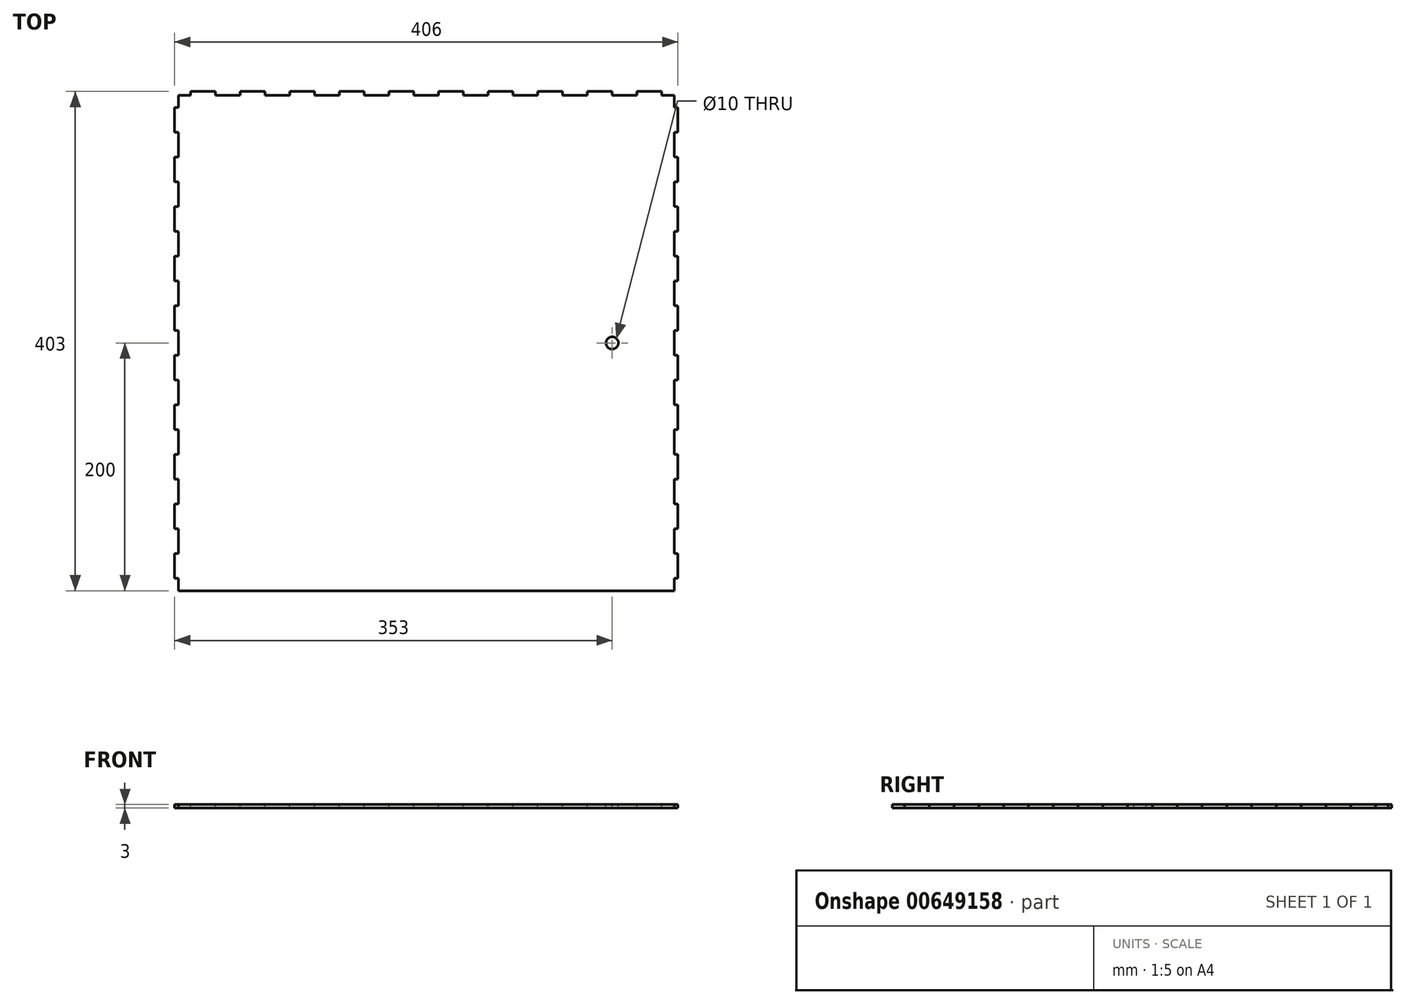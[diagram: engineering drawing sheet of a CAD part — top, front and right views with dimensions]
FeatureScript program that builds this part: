
annotation { "Feature Type Name" : "Feature", "Feature Type Description" : "" }
export const myFeature = defineFeature(function(context is Context, id is Id, definition is map)
    precondition{}
    {
        {
            var Q0;
            Q0=qCreatedBy(makeId("Top.planeOp"),FACE);
            var sketch = newSketch(context, id + "F0", { "sketchPlane" : qUnion([Q0])});
            skLineSegment(sketch, "E0.bottom", {"start": v(200, -200) * mm, "end": v(-200, -200) * mm});
            skLineSegment(sketch, "E0.top", {"start": v(200, 200) * mm, "end": v(-200, 200) * mm});
            skLineSegment(sketch, "E0.left", {"start": v(200, -200) * mm, "end": v(200, 200) * mm});
            skLineSegment(sketch, "E0.right", {"start": v(-200, -200) * mm, "end": v(-200, 200) * mm});
            skPoint(sketch, "E0.middle", {"position": v(0, 0) * mm});
            skSolve(sketch);
        }
        {
            var Q0;
            Q0=makeQuery(id+"F0.imprint","IMPRINT",FACE,{"disambiguationData":[TD([[makeQuery(id+"F0.imprint","IMPRINT",EDGE,{"derivedFrom":sQuery(id+"F0.wireOp",EDGE,"E0.bottom")}),-1.0]])]});
            extrude(context, id + "F1", {"entities" : qUnion([Q0]), "depth" : 3 * mm, "offsetDistance" : 25 * mm});
        }
        {
            var Q0;
            Q0=makeQuery(id+"F1.opExtrude","CAP_FACE",FACE,{"disambiguationData":[OSD([sQuery(id+"F0.wireOp",EDGE,"E0.bottom"),sQuery(id+"F0.wireOp",EDGE,"E0.top"),sQuery(id+"F0.wireOp",EDGE,"E0.left"),sQuery(id+"F0.wireOp",EDGE,"E0.right")])],"isStart":false});
            var sketch = newSketch(context, id + "F2", { "sketchPlane" : qUnion([Q0])});
            skLineSegment(sketch, "E1", {"start": v(-200, -200) * mm, "end": v(-190, -200) * mm, "construction": true});
            skLineSegment(sketch, "E2.bottom", {"start": v(-190, -200) * mm, "end": v(-170, -200) * mm});
            skLineSegment(sketch, "E2.top", {"start": v(-190, -203) * mm, "end": v(-170, -203) * mm});
            skLineSegment(sketch, "E2.left", {"start": v(-190, -200) * mm, "end": v(-190, -203) * mm});
            skLineSegment(sketch, "E2.right", {"start": v(-170, -200) * mm, "end": v(-170, -203) * mm});
            skLineSegment(sketch, "E3.1.0.0", {"start": v(-150, -200) * mm, "end": v(-150, -203) * mm});
            skLineSegment(sketch, "E3.1.0.1", {"start": v(-150, -200) * mm, "end": v(-130, -200) * mm});
            skLineSegment(sketch, "E3.1.0.2", {"start": v(-150, -203) * mm, "end": v(-130, -203) * mm});
            skLineSegment(sketch, "E3.1.0.3", {"start": v(-130, -200) * mm, "end": v(-130, -203) * mm});
            skLineSegment(sketch, "E3.2.0.0", {"start": v(-110, -200) * mm, "end": v(-110, -203) * mm});
            skLineSegment(sketch, "E3.2.0.1", {"start": v(-110, -200) * mm, "end": v(-90, -200) * mm});
            skLineSegment(sketch, "E3.2.0.2", {"start": v(-110, -203) * mm, "end": v(-90, -203) * mm});
            skLineSegment(sketch, "E3.2.0.3", {"start": v(-90, -200) * mm, "end": v(-90, -203) * mm});
            skLineSegment(sketch, "E3.3.0.0", {"start": v(-70, -200) * mm, "end": v(-70, -203) * mm});
            skLineSegment(sketch, "E3.3.0.1", {"start": v(-70, -200) * mm, "end": v(-50, -200) * mm});
            skLineSegment(sketch, "E3.3.0.2", {"start": v(-70, -203) * mm, "end": v(-50, -203) * mm});
            skLineSegment(sketch, "E3.3.0.3", {"start": v(-50, -200) * mm, "end": v(-50, -203) * mm});
            skLineSegment(sketch, "E3.4.0.0", {"start": v(-30, -200) * mm, "end": v(-30, -203) * mm});
            skLineSegment(sketch, "E3.4.0.1", {"start": v(-30, -200) * mm, "end": v(-10, -200) * mm});
            skLineSegment(sketch, "E3.4.0.2", {"start": v(-30, -203) * mm, "end": v(-10, -203) * mm});
            skLineSegment(sketch, "E3.4.0.3", {"start": v(-10, -200) * mm, "end": v(-10, -203) * mm});
            skLineSegment(sketch, "E3.5.0.0", {"start": v(10, -200) * mm, "end": v(10, -203) * mm});
            skLineSegment(sketch, "E3.5.0.1", {"start": v(10, -200) * mm, "end": v(30, -200) * mm});
            skLineSegment(sketch, "E3.5.0.2", {"start": v(10, -203) * mm, "end": v(30, -203) * mm});
            skLineSegment(sketch, "E3.5.0.3", {"start": v(30, -200) * mm, "end": v(30, -203) * mm});
            skLineSegment(sketch, "E3.6.0.0", {"start": v(50, -200) * mm, "end": v(50, -203) * mm});
            skLineSegment(sketch, "E3.6.0.1", {"start": v(50, -200) * mm, "end": v(70, -200) * mm});
            skLineSegment(sketch, "E3.6.0.2", {"start": v(50, -203) * mm, "end": v(70, -203) * mm});
            skLineSegment(sketch, "E3.6.0.3", {"start": v(70, -200) * mm, "end": v(70, -203) * mm});
            skLineSegment(sketch, "E3.7.0.0", {"start": v(90, -200) * mm, "end": v(90, -203) * mm});
            skLineSegment(sketch, "E3.7.0.1", {"start": v(90, -200) * mm, "end": v(110, -200) * mm});
            skLineSegment(sketch, "E3.7.0.2", {"start": v(90, -203) * mm, "end": v(110, -203) * mm});
            skLineSegment(sketch, "E3.7.0.3", {"start": v(110, -200) * mm, "end": v(110, -203) * mm});
            skLineSegment(sketch, "E3.8.0.0", {"start": v(130, -200) * mm, "end": v(130, -203) * mm});
            skLineSegment(sketch, "E3.8.0.1", {"start": v(130, -200) * mm, "end": v(150, -200) * mm});
            skLineSegment(sketch, "E3.8.0.2", {"start": v(130, -203) * mm, "end": v(150, -203) * mm});
            skLineSegment(sketch, "E3.8.0.3", {"start": v(150, -200) * mm, "end": v(150, -203) * mm});
            skLineSegment(sketch, "E3.9.0.0", {"start": v(170, -200) * mm, "end": v(170, -203) * mm});
            skLineSegment(sketch, "E3.9.0.1", {"start": v(170, -200) * mm, "end": v(190, -200) * mm});
            skLineSegment(sketch, "E3.9.0.2", {"start": v(170, -203) * mm, "end": v(190, -203) * mm});
            skLineSegment(sketch, "E3.9.0.3", {"start": v(190, -200) * mm, "end": v(190, -203) * mm});
            skLineSegment(sketch, "E3.direction1", {"start": v(-190, -203) * mm, "end": v(-150, -203) * mm, "construction": true});
            skLineSegment(sketch, "E4.1.0", {"start": v(200, 90) * mm, "end": v(200, 110) * mm});
            skLineSegment(sketch, "E4.1.1", {"start": v(200, 170) * mm, "end": v(203, 170) * mm});
            skLineSegment(sketch, "E4.1.2", {"start": v(200, 10) * mm, "end": v(203, 10) * mm});
            skLineSegment(sketch, "E4.1.3", {"start": v(200, 130) * mm, "end": v(203, 130) * mm});
            skLineSegment(sketch, "E4.1.4", {"start": v(200, -30) * mm, "end": v(203, -30) * mm});
            skLineSegment(sketch, "E4.1.5", {"start": v(203, -190) * mm, "end": v(203, -150) * mm, "construction": true});
            skLineSegment(sketch, "E4.1.6", {"start": v(200, 170) * mm, "end": v(200, 190) * mm});
            skLineSegment(sketch, "E4.1.7", {"start": v(203, 90) * mm, "end": v(203, 110) * mm});
            skLineSegment(sketch, "E4.1.8", {"start": v(200, 10) * mm, "end": v(200, 30) * mm});
            skLineSegment(sketch, "E4.1.9", {"start": v(200, 130) * mm, "end": v(200, 150) * mm});
            skLineSegment(sketch, "E4.1.10", {"start": v(200, -30) * mm, "end": v(200, -10) * mm});
            skLineSegment(sketch, "E4.1.11", {"start": v(200, 50) * mm, "end": v(200, 70) * mm});
            skLineSegment(sketch, "E4.1.12", {"start": v(200, -70) * mm, "end": v(200, -50) * mm});
            skLineSegment(sketch, "E4.1.13", {"start": v(203, -70) * mm, "end": v(203, -50) * mm});
            skLineSegment(sketch, "E4.1.14", {"start": v(200, -190) * mm, "end": v(200, -170) * mm});
            skLineSegment(sketch, "E4.1.15", {"start": v(200, -170) * mm, "end": v(203, -170) * mm});
            skLineSegment(sketch, "E4.1.16", {"start": v(203, 130) * mm, "end": v(203, 150) * mm});
            skLineSegment(sketch, "E4.1.17", {"start": v(203, -30) * mm, "end": v(203, -10) * mm});
            skLineSegment(sketch, "E4.1.18", {"start": v(200, -150) * mm, "end": v(200, -130) * mm});
            skLineSegment(sketch, "E4.1.19", {"start": v(203, -150) * mm, "end": v(203, -130) * mm});
            skLineSegment(sketch, "E4.1.20", {"start": v(200, -130) * mm, "end": v(203, -130) * mm});
            skLineSegment(sketch, "E4.1.21", {"start": v(200, -110) * mm, "end": v(200, -90) * mm});
            skLineSegment(sketch, "E4.1.22", {"start": v(203, -110) * mm, "end": v(203, -90) * mm});
            skLineSegment(sketch, "E4.1.23", {"start": v(200, -90) * mm, "end": v(203, -90) * mm});
            skLineSegment(sketch, "E4.1.24", {"start": v(200, 110) * mm, "end": v(203, 110) * mm});
            skLineSegment(sketch, "E4.1.25", {"start": v(200, -50) * mm, "end": v(203, -50) * mm});
            skLineSegment(sketch, "E4.1.26", {"start": v(203, 50) * mm, "end": v(203, 70) * mm});
            skLineSegment(sketch, "E4.1.27", {"start": v(203, 170) * mm, "end": v(203, 190) * mm});
            skLineSegment(sketch, "E4.1.28", {"start": v(203, 10) * mm, "end": v(203, 30) * mm});
            skLineSegment(sketch, "E4.1.29", {"start": v(200, 150) * mm, "end": v(203, 150) * mm});
            skLineSegment(sketch, "E4.1.30", {"start": v(200, -10) * mm, "end": v(203, -10) * mm});
            skLineSegment(sketch, "E4.1.31", {"start": v(200, 90) * mm, "end": v(203, 90) * mm});
            skLineSegment(sketch, "E4.1.32", {"start": v(200, 70) * mm, "end": v(203, 70) * mm});
            skLineSegment(sketch, "E4.1.33", {"start": v(200, 190) * mm, "end": v(203, 190) * mm});
            skLineSegment(sketch, "E4.1.34", {"start": v(200, 30) * mm, "end": v(203, 30) * mm});
            skLineSegment(sketch, "E4.1.35", {"start": v(200, 50) * mm, "end": v(203, 50) * mm});
            skLineSegment(sketch, "E4.1.36", {"start": v(200, -70) * mm, "end": v(203, -70) * mm});
            skLineSegment(sketch, "E4.1.37", {"start": v(203, -190) * mm, "end": v(203, -170) * mm});
            skLineSegment(sketch, "E4.1.38", {"start": v(200, -150) * mm, "end": v(203, -150) * mm});
            skLineSegment(sketch, "E4.1.39", {"start": v(200, -110) * mm, "end": v(203, -110) * mm});
            skLineSegment(sketch, "E4.1.40", {"start": v(200, -200) * mm, "end": v(200, -190) * mm, "construction": true});
            skLineSegment(sketch, "E4.1.41", {"start": v(200, -190) * mm, "end": v(203, -190) * mm});
            skLineSegment(sketch, "E4.2.0", {"start": v(-90, 200) * mm, "end": v(-110, 200) * mm});
            skLineSegment(sketch, "E4.2.1", {"start": v(-170, 200) * mm, "end": v(-170, 203) * mm});
            skLineSegment(sketch, "E4.2.2", {"start": v(-10, 200) * mm, "end": v(-10, 203) * mm});
            skLineSegment(sketch, "E4.2.3", {"start": v(-130, 200) * mm, "end": v(-130, 203) * mm});
            skLineSegment(sketch, "E4.2.4", {"start": v(30, 200) * mm, "end": v(30, 203) * mm});
            skLineSegment(sketch, "E4.2.5", {"start": v(190, 203) * mm, "end": v(150, 203) * mm, "construction": true});
            skLineSegment(sketch, "E4.2.6", {"start": v(-170, 200) * mm, "end": v(-190, 200) * mm});
            skLineSegment(sketch, "E4.2.7", {"start": v(-90, 203) * mm, "end": v(-110, 203) * mm});
            skLineSegment(sketch, "E4.2.8", {"start": v(-10, 200) * mm, "end": v(-30, 200) * mm});
            skLineSegment(sketch, "E4.2.9", {"start": v(-130, 200) * mm, "end": v(-150, 200) * mm});
            skLineSegment(sketch, "E4.2.10", {"start": v(30, 200) * mm, "end": v(10, 200) * mm});
            skLineSegment(sketch, "E4.2.11", {"start": v(-50, 200) * mm, "end": v(-70, 200) * mm});
            skLineSegment(sketch, "E4.2.12", {"start": v(70, 200) * mm, "end": v(50, 200) * mm});
            skLineSegment(sketch, "E4.2.13", {"start": v(70, 203) * mm, "end": v(50, 203) * mm});
            skLineSegment(sketch, "E4.2.14", {"start": v(190, 200) * mm, "end": v(170, 200) * mm});
            skLineSegment(sketch, "E4.2.15", {"start": v(170, 200) * mm, "end": v(170, 203) * mm});
            skLineSegment(sketch, "E4.2.16", {"start": v(-130, 203) * mm, "end": v(-150, 203) * mm});
            skLineSegment(sketch, "E4.2.17", {"start": v(30, 203) * mm, "end": v(10, 203) * mm});
            skLineSegment(sketch, "E4.2.18", {"start": v(150, 200) * mm, "end": v(130, 200) * mm});
            skLineSegment(sketch, "E4.2.19", {"start": v(150, 203) * mm, "end": v(130, 203) * mm});
            skLineSegment(sketch, "E4.2.20", {"start": v(130, 200) * mm, "end": v(130, 203) * mm});
            skLineSegment(sketch, "E4.2.21", {"start": v(110, 200) * mm, "end": v(90, 200) * mm});
            skLineSegment(sketch, "E4.2.22", {"start": v(110, 203) * mm, "end": v(90, 203) * mm});
            skLineSegment(sketch, "E4.2.23", {"start": v(90, 200) * mm, "end": v(90, 203) * mm});
            skLineSegment(sketch, "E4.2.24", {"start": v(-110, 200) * mm, "end": v(-110, 203) * mm});
            skLineSegment(sketch, "E4.2.25", {"start": v(50, 200) * mm, "end": v(50, 203) * mm});
            skLineSegment(sketch, "E4.2.26", {"start": v(-50, 203) * mm, "end": v(-70, 203) * mm});
            skLineSegment(sketch, "E4.2.27", {"start": v(-170, 203) * mm, "end": v(-190, 203) * mm});
            skLineSegment(sketch, "E4.2.28", {"start": v(-10, 203) * mm, "end": v(-30, 203) * mm});
            skLineSegment(sketch, "E4.2.29", {"start": v(-150, 200) * mm, "end": v(-150, 203) * mm});
            skLineSegment(sketch, "E4.2.30", {"start": v(10, 200) * mm, "end": v(10, 203) * mm});
            skLineSegment(sketch, "E4.2.31", {"start": v(-90, 200) * mm, "end": v(-90, 203) * mm});
            skLineSegment(sketch, "E4.2.32", {"start": v(-70, 200) * mm, "end": v(-70, 203) * mm});
            skLineSegment(sketch, "E4.2.33", {"start": v(-190, 200) * mm, "end": v(-190, 203) * mm});
            skLineSegment(sketch, "E4.2.34", {"start": v(-30, 200) * mm, "end": v(-30, 203) * mm});
            skLineSegment(sketch, "E4.2.35", {"start": v(-50, 200) * mm, "end": v(-50, 203) * mm});
            skLineSegment(sketch, "E4.2.36", {"start": v(70, 200) * mm, "end": v(70, 203) * mm});
            skLineSegment(sketch, "E4.2.37", {"start": v(190, 203) * mm, "end": v(170, 203) * mm});
            skLineSegment(sketch, "E4.2.38", {"start": v(150, 200) * mm, "end": v(150, 203) * mm});
            skLineSegment(sketch, "E4.2.39", {"start": v(110, 200) * mm, "end": v(110, 203) * mm});
            skLineSegment(sketch, "E4.2.40", {"start": v(200, 200) * mm, "end": v(190, 200) * mm, "construction": true});
            skLineSegment(sketch, "E4.2.41", {"start": v(190, 200) * mm, "end": v(190, 203) * mm});
            skLineSegment(sketch, "E4.3.0", {"start": v(-200, -90) * mm, "end": v(-200, -110) * mm});
            skLineSegment(sketch, "E4.3.1", {"start": v(-200, -170) * mm, "end": v(-203, -170) * mm});
            skLineSegment(sketch, "E4.3.2", {"start": v(-200, -10) * mm, "end": v(-203, -10) * mm});
            skLineSegment(sketch, "E4.3.3", {"start": v(-200, -130) * mm, "end": v(-203, -130) * mm});
            skLineSegment(sketch, "E4.3.4", {"start": v(-200, 30) * mm, "end": v(-203, 30) * mm});
            skLineSegment(sketch, "E4.3.5", {"start": v(-203, 190) * mm, "end": v(-203, 150) * mm, "construction": true});
            skLineSegment(sketch, "E4.3.6", {"start": v(-200, -170) * mm, "end": v(-200, -190) * mm});
            skLineSegment(sketch, "E4.3.7", {"start": v(-203, -90) * mm, "end": v(-203, -110) * mm});
            skLineSegment(sketch, "E4.3.8", {"start": v(-200, -10) * mm, "end": v(-200, -30) * mm});
            skLineSegment(sketch, "E4.3.9", {"start": v(-200, -130) * mm, "end": v(-200, -150) * mm});
            skLineSegment(sketch, "E4.3.10", {"start": v(-200, 30) * mm, "end": v(-200, 10) * mm});
            skLineSegment(sketch, "E4.3.11", {"start": v(-200, -50) * mm, "end": v(-200, -70) * mm});
            skLineSegment(sketch, "E4.3.12", {"start": v(-200, 70) * mm, "end": v(-200, 50) * mm});
            skLineSegment(sketch, "E4.3.13", {"start": v(-203, 70) * mm, "end": v(-203, 50) * mm});
            skLineSegment(sketch, "E4.3.14", {"start": v(-200, 190) * mm, "end": v(-200, 170) * mm});
            skLineSegment(sketch, "E4.3.15", {"start": v(-200, 170) * mm, "end": v(-203, 170) * mm});
            skLineSegment(sketch, "E4.3.16", {"start": v(-203, -130) * mm, "end": v(-203, -150) * mm});
            skLineSegment(sketch, "E4.3.17", {"start": v(-203, 30) * mm, "end": v(-203, 10) * mm});
            skLineSegment(sketch, "E4.3.18", {"start": v(-200, 150) * mm, "end": v(-200, 130) * mm});
            skLineSegment(sketch, "E4.3.19", {"start": v(-203, 150) * mm, "end": v(-203, 130) * mm});
            skLineSegment(sketch, "E4.3.20", {"start": v(-200, 130) * mm, "end": v(-203, 130) * mm});
            skLineSegment(sketch, "E4.3.21", {"start": v(-200, 110) * mm, "end": v(-200, 90) * mm});
            skLineSegment(sketch, "E4.3.22", {"start": v(-203, 110) * mm, "end": v(-203, 90) * mm});
            skLineSegment(sketch, "E4.3.23", {"start": v(-200, 90) * mm, "end": v(-203, 90) * mm});
            skLineSegment(sketch, "E4.3.24", {"start": v(-200, -110) * mm, "end": v(-203, -110) * mm});
            skLineSegment(sketch, "E4.3.25", {"start": v(-200, 50) * mm, "end": v(-203, 50) * mm});
            skLineSegment(sketch, "E4.3.26", {"start": v(-203, -50) * mm, "end": v(-203, -70) * mm});
            skLineSegment(sketch, "E4.3.27", {"start": v(-203, -170) * mm, "end": v(-203, -190) * mm});
            skLineSegment(sketch, "E4.3.28", {"start": v(-203, -10) * mm, "end": v(-203, -30) * mm});
            skLineSegment(sketch, "E4.3.29", {"start": v(-200, -150) * mm, "end": v(-203, -150) * mm});
            skLineSegment(sketch, "E4.3.30", {"start": v(-200, 10) * mm, "end": v(-203, 10) * mm});
            skLineSegment(sketch, "E4.3.31", {"start": v(-200, -90) * mm, "end": v(-203, -90) * mm});
            skLineSegment(sketch, "E4.3.32", {"start": v(-200, -70) * mm, "end": v(-203, -70) * mm});
            skLineSegment(sketch, "E4.3.33", {"start": v(-200, -190) * mm, "end": v(-203, -190) * mm});
            skLineSegment(sketch, "E4.3.34", {"start": v(-200, -30) * mm, "end": v(-203, -30) * mm});
            skLineSegment(sketch, "E4.3.35", {"start": v(-200, -50) * mm, "end": v(-203, -50) * mm});
            skLineSegment(sketch, "E4.3.36", {"start": v(-200, 70) * mm, "end": v(-203, 70) * mm});
            skLineSegment(sketch, "E4.3.37", {"start": v(-203, 190) * mm, "end": v(-203, 170) * mm});
            skLineSegment(sketch, "E4.3.38", {"start": v(-200, 150) * mm, "end": v(-203, 150) * mm});
            skLineSegment(sketch, "E4.3.39", {"start": v(-200, 110) * mm, "end": v(-203, 110) * mm});
            skLineSegment(sketch, "E4.3.40", {"start": v(-200, 200) * mm, "end": v(-200, 190) * mm, "construction": true});
            skLineSegment(sketch, "E4.3.41", {"start": v(-200, 190) * mm, "end": v(-203, 190) * mm});
            skPoint(sketch, "E4.center", {"position": v(0, 0) * mm});
            skSolve(sketch);
        }
        {
            var Q0;
            Q0 = qSketchRegion(id + "F2", true);
            var Q1;
            Q1=makeQuery(id+"F1.opExtrude","CAP_FACE",FACE,{"disambiguationData":[OSD([sQuery(id+"F0.wireOp",EDGE,"E0.bottom"),sQuery(id+"F0.wireOp",EDGE,"E0.top"),sQuery(id+"F0.wireOp",EDGE,"E0.left"),sQuery(id+"F0.wireOp",EDGE,"E0.right")])],"isStart":true});
            extrude(context, id + "F3", {"entities" : qUnion([Q0]), "operationType" : NewBodyOperationType.ADD, "endBound" : BoundingType.UP_TO_SURFACE, "oppositeDirection" : true, "depth" : 25 * mm, "endBoundEntityFace" : qUnion([Q1]), "offsetDistance" : 25 * mm});
        }
        {
            var Q0;
            Q0=makeQuery(id+"F3.boolean.opBoolean","MERGE",FACE,{"derivedFrom":[makeQuery(id+"F1.opExtrude","CAP_FACE",FACE,{"disambiguationData":[OSD([sQuery(id+"F0.wireOp",EDGE,"E0.bottom"),sQuery(id+"F0.wireOp",EDGE,"E0.top"),sQuery(id+"F0.wireOp",EDGE,"E0.left"),sQuery(id+"F0.wireOp",EDGE,"E0.right")])],"isStart":false}),makeQuery(id+"F3.opExtrude","CAP_FACE",FACE,{"disambiguationData":[OSD([sQuery(id+"F2.wireOp",EDGE,"E2.bottom"),sQuery(id+"F2.wireOp",EDGE,"E2.top"),sQuery(id+"F2.wireOp",EDGE,"E2.left"),sQuery(id+"F2.wireOp",EDGE,"E2.right")])],"isStart":true}),makeQuery(id+"F3.opExtrude","CAP_FACE",FACE,{"disambiguationData":[OSD([sQuery(id+"F2.wireOp",EDGE,"E3.1.0.0"),sQuery(id+"F2.wireOp",EDGE,"E3.1.0.1"),sQuery(id+"F2.wireOp",EDGE,"E3.1.0.2"),sQuery(id+"F2.wireOp",EDGE,"E3.1.0.3")])],"isStart":true}),makeQuery(id+"F3.opExtrude","CAP_FACE",FACE,{"disambiguationData":[OSD([sQuery(id+"F2.wireOp",EDGE,"E3.2.0.0"),sQuery(id+"F2.wireOp",EDGE,"E3.2.0.1"),sQuery(id+"F2.wireOp",EDGE,"E3.2.0.2"),sQuery(id+"F2.wireOp",EDGE,"E3.2.0.3")])],"isStart":true}),makeQuery(id+"F3.opExtrude","CAP_FACE",FACE,{"disambiguationData":[OSD([sQuery(id+"F2.wireOp",EDGE,"E3.3.0.0"),sQuery(id+"F2.wireOp",EDGE,"E3.3.0.1"),sQuery(id+"F2.wireOp",EDGE,"E3.3.0.2"),sQuery(id+"F2.wireOp",EDGE,"E3.3.0.3")])],"isStart":true}),makeQuery(id+"F3.opExtrude","CAP_FACE",FACE,{"disambiguationData":[OSD([sQuery(id+"F2.wireOp",EDGE,"E3.4.0.0"),sQuery(id+"F2.wireOp",EDGE,"E3.4.0.1"),sQuery(id+"F2.wireOp",EDGE,"E3.4.0.2"),sQuery(id+"F2.wireOp",EDGE,"E3.4.0.3")])],"isStart":true}),makeQuery(id+"F3.opExtrude","CAP_FACE",FACE,{"disambiguationData":[OSD([sQuery(id+"F2.wireOp",EDGE,"E3.5.0.0"),sQuery(id+"F2.wireOp",EDGE,"E3.5.0.1"),sQuery(id+"F2.wireOp",EDGE,"E3.5.0.2"),sQuery(id+"F2.wireOp",EDGE,"E3.5.0.3")])],"isStart":true}),makeQuery(id+"F3.opExtrude","CAP_FACE",FACE,{"disambiguationData":[OSD([sQuery(id+"F2.wireOp",EDGE,"E3.6.0.0"),sQuery(id+"F2.wireOp",EDGE,"E3.6.0.1"),sQuery(id+"F2.wireOp",EDGE,"E3.6.0.2"),sQuery(id+"F2.wireOp",EDGE,"E3.6.0.3")])],"isStart":true}),makeQuery(id+"F3.opExtrude","CAP_FACE",FACE,{"disambiguationData":[OSD([sQuery(id+"F2.wireOp",EDGE,"E3.7.0.0"),sQuery(id+"F2.wireOp",EDGE,"E3.7.0.1"),sQuery(id+"F2.wireOp",EDGE,"E3.7.0.2"),sQuery(id+"F2.wireOp",EDGE,"E3.7.0.3")])],"isStart":true}),makeQuery(id+"F3.opExtrude","CAP_FACE",FACE,{"disambiguationData":[OSD([sQuery(id+"F2.wireOp",EDGE,"E3.8.0.0"),sQuery(id+"F2.wireOp",EDGE,"E3.8.0.1"),sQuery(id+"F2.wireOp",EDGE,"E3.8.0.2"),sQuery(id+"F2.wireOp",EDGE,"E3.8.0.3")])],"isStart":true}),makeQuery(id+"F3.opExtrude","CAP_FACE",FACE,{"disambiguationData":[OSD([sQuery(id+"F2.wireOp",EDGE,"E3.9.0.0"),sQuery(id+"F2.wireOp",EDGE,"E3.9.0.1"),sQuery(id+"F2.wireOp",EDGE,"E3.9.0.2"),sQuery(id+"F2.wireOp",EDGE,"E3.9.0.3")])],"isStart":true}),makeQuery(id+"F3.opExtrude","CAP_FACE",FACE,{"disambiguationData":[OSD([sQuery(id+"F2.wireOp",EDGE,"E4.1.0"),sQuery(id+"F2.wireOp",EDGE,"E4.1.7"),sQuery(id+"F2.wireOp",EDGE,"E4.1.24"),sQuery(id+"F2.wireOp",EDGE,"E4.1.31")])],"isStart":true}),makeQuery(id+"F3.opExtrude","CAP_FACE",FACE,{"disambiguationData":[OSD([sQuery(id+"F2.wireOp",EDGE,"E4.1.1"),sQuery(id+"F2.wireOp",EDGE,"E4.1.6"),sQuery(id+"F2.wireOp",EDGE,"E4.1.27"),sQuery(id+"F2.wireOp",EDGE,"E4.1.33")])],"isStart":true}),makeQuery(id+"F3.opExtrude","CAP_FACE",FACE,{"disambiguationData":[OSD([sQuery(id+"F2.wireOp",EDGE,"E4.1.2"),sQuery(id+"F2.wireOp",EDGE,"E4.1.8"),sQuery(id+"F2.wireOp",EDGE,"E4.1.28"),sQuery(id+"F2.wireOp",EDGE,"E4.1.34")])],"isStart":true}),makeQuery(id+"F3.opExtrude","CAP_FACE",FACE,{"disambiguationData":[OSD([sQuery(id+"F2.wireOp",EDGE,"E4.1.3"),sQuery(id+"F2.wireOp",EDGE,"E4.1.9"),sQuery(id+"F2.wireOp",EDGE,"E4.1.16"),sQuery(id+"F2.wireOp",EDGE,"E4.1.29")])],"isStart":true}),makeQuery(id+"F3.opExtrude","CAP_FACE",FACE,{"disambiguationData":[OSD([sQuery(id+"F2.wireOp",EDGE,"E4.1.4"),sQuery(id+"F2.wireOp",EDGE,"E4.1.10"),sQuery(id+"F2.wireOp",EDGE,"E4.1.17"),sQuery(id+"F2.wireOp",EDGE,"E4.1.30")])],"isStart":true}),makeQuery(id+"F3.opExtrude","CAP_FACE",FACE,{"disambiguationData":[OSD([sQuery(id+"F2.wireOp",EDGE,"E4.1.11"),sQuery(id+"F2.wireOp",EDGE,"E4.1.26"),sQuery(id+"F2.wireOp",EDGE,"E4.1.32"),sQuery(id+"F2.wireOp",EDGE,"E4.1.35")])],"isStart":true}),makeQuery(id+"F3.opExtrude","CAP_FACE",FACE,{"disambiguationData":[OSD([sQuery(id+"F2.wireOp",EDGE,"E4.1.12"),sQuery(id+"F2.wireOp",EDGE,"E4.1.13"),sQuery(id+"F2.wireOp",EDGE,"E4.1.25"),sQuery(id+"F2.wireOp",EDGE,"E4.1.36")])],"isStart":true}),makeQuery(id+"F3.opExtrude","CAP_FACE",FACE,{"disambiguationData":[OSD([sQuery(id+"F2.wireOp",EDGE,"E4.1.14"),sQuery(id+"F2.wireOp",EDGE,"E4.1.15"),sQuery(id+"F2.wireOp",EDGE,"E4.1.37"),sQuery(id+"F2.wireOp",EDGE,"E4.1.41")])],"isStart":true}),makeQuery(id+"F3.opExtrude","CAP_FACE",FACE,{"disambiguationData":[OSD([sQuery(id+"F2.wireOp",EDGE,"E4.1.18"),sQuery(id+"F2.wireOp",EDGE,"E4.1.19"),sQuery(id+"F2.wireOp",EDGE,"E4.1.20"),sQuery(id+"F2.wireOp",EDGE,"E4.1.38")])],"isStart":true}),makeQuery(id+"F3.opExtrude","CAP_FACE",FACE,{"disambiguationData":[OSD([sQuery(id+"F2.wireOp",EDGE,"E4.1.21"),sQuery(id+"F2.wireOp",EDGE,"E4.1.22"),sQuery(id+"F2.wireOp",EDGE,"E4.1.23"),sQuery(id+"F2.wireOp",EDGE,"E4.1.39")])],"isStart":true}),makeQuery(id+"F3.opExtrude","CAP_FACE",FACE,{"disambiguationData":[OSD([sQuery(id+"F2.wireOp",EDGE,"E4.2.0"),sQuery(id+"F2.wireOp",EDGE,"E4.2.7"),sQuery(id+"F2.wireOp",EDGE,"E4.2.24"),sQuery(id+"F2.wireOp",EDGE,"E4.2.31")])],"isStart":true}),makeQuery(id+"F3.opExtrude","CAP_FACE",FACE,{"disambiguationData":[OSD([sQuery(id+"F2.wireOp",EDGE,"E4.2.1"),sQuery(id+"F2.wireOp",EDGE,"E4.2.6"),sQuery(id+"F2.wireOp",EDGE,"E4.2.27"),sQuery(id+"F2.wireOp",EDGE,"E4.2.33")])],"isStart":true}),makeQuery(id+"F3.opExtrude","CAP_FACE",FACE,{"disambiguationData":[OSD([sQuery(id+"F2.wireOp",EDGE,"E4.2.2"),sQuery(id+"F2.wireOp",EDGE,"E4.2.8"),sQuery(id+"F2.wireOp",EDGE,"E4.2.28"),sQuery(id+"F2.wireOp",EDGE,"E4.2.34")])],"isStart":true}),makeQuery(id+"F3.opExtrude","CAP_FACE",FACE,{"disambiguationData":[OSD([sQuery(id+"F2.wireOp",EDGE,"E4.2.3"),sQuery(id+"F2.wireOp",EDGE,"E4.2.9"),sQuery(id+"F2.wireOp",EDGE,"E4.2.16"),sQuery(id+"F2.wireOp",EDGE,"E4.2.29")])],"isStart":true}),makeQuery(id+"F3.opExtrude","CAP_FACE",FACE,{"disambiguationData":[OSD([sQuery(id+"F2.wireOp",EDGE,"E4.2.4"),sQuery(id+"F2.wireOp",EDGE,"E4.2.10"),sQuery(id+"F2.wireOp",EDGE,"E4.2.17"),sQuery(id+"F2.wireOp",EDGE,"E4.2.30")])],"isStart":true}),makeQuery(id+"F3.opExtrude","CAP_FACE",FACE,{"disambiguationData":[OSD([sQuery(id+"F2.wireOp",EDGE,"E4.2.11"),sQuery(id+"F2.wireOp",EDGE,"E4.2.26"),sQuery(id+"F2.wireOp",EDGE,"E4.2.32"),sQuery(id+"F2.wireOp",EDGE,"E4.2.35")])],"isStart":true}),makeQuery(id+"F3.opExtrude","CAP_FACE",FACE,{"disambiguationData":[OSD([sQuery(id+"F2.wireOp",EDGE,"E4.2.12"),sQuery(id+"F2.wireOp",EDGE,"E4.2.13"),sQuery(id+"F2.wireOp",EDGE,"E4.2.25"),sQuery(id+"F2.wireOp",EDGE,"E4.2.36")])],"isStart":true}),makeQuery(id+"F3.opExtrude","CAP_FACE",FACE,{"disambiguationData":[OSD([sQuery(id+"F2.wireOp",EDGE,"E4.2.14"),sQuery(id+"F2.wireOp",EDGE,"E4.2.15"),sQuery(id+"F2.wireOp",EDGE,"E4.2.37"),sQuery(id+"F2.wireOp",EDGE,"E4.2.41")])],"isStart":true}),makeQuery(id+"F3.opExtrude","CAP_FACE",FACE,{"disambiguationData":[OSD([sQuery(id+"F2.wireOp",EDGE,"E4.2.18"),sQuery(id+"F2.wireOp",EDGE,"E4.2.19"),sQuery(id+"F2.wireOp",EDGE,"E4.2.20"),sQuery(id+"F2.wireOp",EDGE,"E4.2.38")])],"isStart":true}),makeQuery(id+"F3.opExtrude","CAP_FACE",FACE,{"disambiguationData":[OSD([sQuery(id+"F2.wireOp",EDGE,"E4.2.21"),sQuery(id+"F2.wireOp",EDGE,"E4.2.22"),sQuery(id+"F2.wireOp",EDGE,"E4.2.23"),sQuery(id+"F2.wireOp",EDGE,"E4.2.39")])],"isStart":true}),makeQuery(id+"F3.opExtrude","CAP_FACE",FACE,{"disambiguationData":[OSD([sQuery(id+"F2.wireOp",EDGE,"E4.3.0"),sQuery(id+"F2.wireOp",EDGE,"E4.3.7"),sQuery(id+"F2.wireOp",EDGE,"E4.3.24"),sQuery(id+"F2.wireOp",EDGE,"E4.3.31")])],"isStart":true}),makeQuery(id+"F3.opExtrude","CAP_FACE",FACE,{"disambiguationData":[OSD([sQuery(id+"F2.wireOp",EDGE,"E4.3.1"),sQuery(id+"F2.wireOp",EDGE,"E4.3.6"),sQuery(id+"F2.wireOp",EDGE,"E4.3.27"),sQuery(id+"F2.wireOp",EDGE,"E4.3.33")])],"isStart":true}),makeQuery(id+"F3.opExtrude","CAP_FACE",FACE,{"disambiguationData":[OSD([sQuery(id+"F2.wireOp",EDGE,"E4.3.2"),sQuery(id+"F2.wireOp",EDGE,"E4.3.8"),sQuery(id+"F2.wireOp",EDGE,"E4.3.28"),sQuery(id+"F2.wireOp",EDGE,"E4.3.34")])],"isStart":true}),makeQuery(id+"F3.opExtrude","CAP_FACE",FACE,{"disambiguationData":[OSD([sQuery(id+"F2.wireOp",EDGE,"E4.3.3"),sQuery(id+"F2.wireOp",EDGE,"E4.3.9"),sQuery(id+"F2.wireOp",EDGE,"E4.3.16"),sQuery(id+"F2.wireOp",EDGE,"E4.3.29")])],"isStart":true}),makeQuery(id+"F3.opExtrude","CAP_FACE",FACE,{"disambiguationData":[OSD([sQuery(id+"F2.wireOp",EDGE,"E4.3.4"),sQuery(id+"F2.wireOp",EDGE,"E4.3.10"),sQuery(id+"F2.wireOp",EDGE,"E4.3.17"),sQuery(id+"F2.wireOp",EDGE,"E4.3.30")])],"isStart":true}),makeQuery(id+"F3.opExtrude","CAP_FACE",FACE,{"disambiguationData":[OSD([sQuery(id+"F2.wireOp",EDGE,"E4.3.11"),sQuery(id+"F2.wireOp",EDGE,"E4.3.26"),sQuery(id+"F2.wireOp",EDGE,"E4.3.32"),sQuery(id+"F2.wireOp",EDGE,"E4.3.35")])],"isStart":true}),makeQuery(id+"F3.opExtrude","CAP_FACE",FACE,{"disambiguationData":[OSD([sQuery(id+"F2.wireOp",EDGE,"E4.3.12"),sQuery(id+"F2.wireOp",EDGE,"E4.3.13"),sQuery(id+"F2.wireOp",EDGE,"E4.3.25"),sQuery(id+"F2.wireOp",EDGE,"E4.3.36")])],"isStart":true}),makeQuery(id+"F3.opExtrude","CAP_FACE",FACE,{"disambiguationData":[OSD([sQuery(id+"F2.wireOp",EDGE,"E4.3.14"),sQuery(id+"F2.wireOp",EDGE,"E4.3.15"),sQuery(id+"F2.wireOp",EDGE,"E4.3.37"),sQuery(id+"F2.wireOp",EDGE,"E4.3.41")])],"isStart":true}),makeQuery(id+"F3.opExtrude","CAP_FACE",FACE,{"disambiguationData":[OSD([sQuery(id+"F2.wireOp",EDGE,"E4.3.18"),sQuery(id+"F2.wireOp",EDGE,"E4.3.19"),sQuery(id+"F2.wireOp",EDGE,"E4.3.20"),sQuery(id+"F2.wireOp",EDGE,"E4.3.38")])],"isStart":true}),makeQuery(id+"F3.opExtrude","CAP_FACE",FACE,{"disambiguationData":[OSD([sQuery(id+"F2.wireOp",EDGE,"E4.3.21"),sQuery(id+"F2.wireOp",EDGE,"E4.3.22"),sQuery(id+"F2.wireOp",EDGE,"E4.3.23"),sQuery(id+"F2.wireOp",EDGE,"E4.3.39")])],"isStart":true})]});
            var sketch = newSketch(context, id + "F4", { "sketchPlane" : qUnion([Q0])});
            skPoint(sketch, "E5.middle", {"position": v(0, 0) * mm});
            skPoint(sketch, "E5.right.start.orphan", {"position": v(-150, 5) * mm});
            skPoint(sketch, "E5.top.end.orphan", {"position": v(-150, -5) * mm});
            skPoint(sketch, "E5.left.end.orphan", {"position": v(150, -5) * mm});
            skPoint(sketch, "E5.left.start.orphan", {"position": v(150, 5) * mm});
            skLineSegment(sketch, "E6", {"start": v(0, 0) * mm, "end": v(150, 0) * mm, "construction": true});
            skCircle(sketch, "E7", {"center": v(150, 0) * mm, "radius": 5 * mm});
            skSolve(sketch);
        }
        {
            var Q0;
            Q0=makeQuery(id+"F4.imprint","IMPRINT",FACE,{"disambiguationData":[TD([[makeQuery(id+"F4.imprint","IMPRINT",EDGE,{"derivedFrom":sQuery(id+"F4.wireOp",EDGE,"E7")}),1.0]])]});
            extrude(context, id + "F5", {"entities" : qUnion([Q0]), "operationType" : NewBodyOperationType.REMOVE, "oppositeDirection" : true, "depth" : 25 * mm, "offsetDistance" : 25 * mm});
        }
        {
            var Q0;
            Q0=makeQuery(id+"F3.boolean.opBoolean","MERGE",FACE,{"derivedFrom":[makeQuery(id+"F1.opExtrude","CAP_FACE",FACE,{"disambiguationData":[OSD([sQuery(id+"F0.wireOp",EDGE,"E0.bottom"),sQuery(id+"F0.wireOp",EDGE,"E0.top"),sQuery(id+"F0.wireOp",EDGE,"E0.left"),sQuery(id+"F0.wireOp",EDGE,"E0.right")])],"isStart":false}),makeQuery(id+"F3.opExtrude","CAP_FACE",FACE,{"disambiguationData":[OSD([sQuery(id+"F2.wireOp",EDGE,"E2.bottom"),sQuery(id+"F2.wireOp",EDGE,"E2.top"),sQuery(id+"F2.wireOp",EDGE,"E2.left"),sQuery(id+"F2.wireOp",EDGE,"E2.right")])],"isStart":true}),makeQuery(id+"F3.opExtrude","CAP_FACE",FACE,{"disambiguationData":[OSD([sQuery(id+"F2.wireOp",EDGE,"E3.1.0.0"),sQuery(id+"F2.wireOp",EDGE,"E3.1.0.1"),sQuery(id+"F2.wireOp",EDGE,"E3.1.0.2"),sQuery(id+"F2.wireOp",EDGE,"E3.1.0.3")])],"isStart":true}),makeQuery(id+"F3.opExtrude","CAP_FACE",FACE,{"disambiguationData":[OSD([sQuery(id+"F2.wireOp",EDGE,"E3.2.0.0"),sQuery(id+"F2.wireOp",EDGE,"E3.2.0.1"),sQuery(id+"F2.wireOp",EDGE,"E3.2.0.2"),sQuery(id+"F2.wireOp",EDGE,"E3.2.0.3")])],"isStart":true}),makeQuery(id+"F3.opExtrude","CAP_FACE",FACE,{"disambiguationData":[OSD([sQuery(id+"F2.wireOp",EDGE,"E3.3.0.0"),sQuery(id+"F2.wireOp",EDGE,"E3.3.0.1"),sQuery(id+"F2.wireOp",EDGE,"E3.3.0.2"),sQuery(id+"F2.wireOp",EDGE,"E3.3.0.3")])],"isStart":true}),makeQuery(id+"F3.opExtrude","CAP_FACE",FACE,{"disambiguationData":[OSD([sQuery(id+"F2.wireOp",EDGE,"E3.4.0.0"),sQuery(id+"F2.wireOp",EDGE,"E3.4.0.1"),sQuery(id+"F2.wireOp",EDGE,"E3.4.0.2"),sQuery(id+"F2.wireOp",EDGE,"E3.4.0.3")])],"isStart":true}),makeQuery(id+"F3.opExtrude","CAP_FACE",FACE,{"disambiguationData":[OSD([sQuery(id+"F2.wireOp",EDGE,"E3.5.0.0"),sQuery(id+"F2.wireOp",EDGE,"E3.5.0.1"),sQuery(id+"F2.wireOp",EDGE,"E3.5.0.2"),sQuery(id+"F2.wireOp",EDGE,"E3.5.0.3")])],"isStart":true}),makeQuery(id+"F3.opExtrude","CAP_FACE",FACE,{"disambiguationData":[OSD([sQuery(id+"F2.wireOp",EDGE,"E3.6.0.0"),sQuery(id+"F2.wireOp",EDGE,"E3.6.0.1"),sQuery(id+"F2.wireOp",EDGE,"E3.6.0.2"),sQuery(id+"F2.wireOp",EDGE,"E3.6.0.3")])],"isStart":true}),makeQuery(id+"F3.opExtrude","CAP_FACE",FACE,{"disambiguationData":[OSD([sQuery(id+"F2.wireOp",EDGE,"E3.7.0.0"),sQuery(id+"F2.wireOp",EDGE,"E3.7.0.1"),sQuery(id+"F2.wireOp",EDGE,"E3.7.0.2"),sQuery(id+"F2.wireOp",EDGE,"E3.7.0.3")])],"isStart":true}),makeQuery(id+"F3.opExtrude","CAP_FACE",FACE,{"disambiguationData":[OSD([sQuery(id+"F2.wireOp",EDGE,"E3.8.0.0"),sQuery(id+"F2.wireOp",EDGE,"E3.8.0.1"),sQuery(id+"F2.wireOp",EDGE,"E3.8.0.2"),sQuery(id+"F2.wireOp",EDGE,"E3.8.0.3")])],"isStart":true}),makeQuery(id+"F3.opExtrude","CAP_FACE",FACE,{"disambiguationData":[OSD([sQuery(id+"F2.wireOp",EDGE,"E3.9.0.0"),sQuery(id+"F2.wireOp",EDGE,"E3.9.0.1"),sQuery(id+"F2.wireOp",EDGE,"E3.9.0.2"),sQuery(id+"F2.wireOp",EDGE,"E3.9.0.3")])],"isStart":true}),makeQuery(id+"F3.opExtrude","CAP_FACE",FACE,{"disambiguationData":[OSD([sQuery(id+"F2.wireOp",EDGE,"E4.1.0"),sQuery(id+"F2.wireOp",EDGE,"E4.1.7"),sQuery(id+"F2.wireOp",EDGE,"E4.1.24"),sQuery(id+"F2.wireOp",EDGE,"E4.1.31")])],"isStart":true}),makeQuery(id+"F3.opExtrude","CAP_FACE",FACE,{"disambiguationData":[OSD([sQuery(id+"F2.wireOp",EDGE,"E4.1.1"),sQuery(id+"F2.wireOp",EDGE,"E4.1.6"),sQuery(id+"F2.wireOp",EDGE,"E4.1.27"),sQuery(id+"F2.wireOp",EDGE,"E4.1.33")])],"isStart":true}),makeQuery(id+"F3.opExtrude","CAP_FACE",FACE,{"disambiguationData":[OSD([sQuery(id+"F2.wireOp",EDGE,"E4.1.2"),sQuery(id+"F2.wireOp",EDGE,"E4.1.8"),sQuery(id+"F2.wireOp",EDGE,"E4.1.28"),sQuery(id+"F2.wireOp",EDGE,"E4.1.34")])],"isStart":true}),makeQuery(id+"F3.opExtrude","CAP_FACE",FACE,{"disambiguationData":[OSD([sQuery(id+"F2.wireOp",EDGE,"E4.1.3"),sQuery(id+"F2.wireOp",EDGE,"E4.1.9"),sQuery(id+"F2.wireOp",EDGE,"E4.1.16"),sQuery(id+"F2.wireOp",EDGE,"E4.1.29")])],"isStart":true}),makeQuery(id+"F3.opExtrude","CAP_FACE",FACE,{"disambiguationData":[OSD([sQuery(id+"F2.wireOp",EDGE,"E4.1.4"),sQuery(id+"F2.wireOp",EDGE,"E4.1.10"),sQuery(id+"F2.wireOp",EDGE,"E4.1.17"),sQuery(id+"F2.wireOp",EDGE,"E4.1.30")])],"isStart":true}),makeQuery(id+"F3.opExtrude","CAP_FACE",FACE,{"disambiguationData":[OSD([sQuery(id+"F2.wireOp",EDGE,"E4.1.11"),sQuery(id+"F2.wireOp",EDGE,"E4.1.26"),sQuery(id+"F2.wireOp",EDGE,"E4.1.32"),sQuery(id+"F2.wireOp",EDGE,"E4.1.35")])],"isStart":true}),makeQuery(id+"F3.opExtrude","CAP_FACE",FACE,{"disambiguationData":[OSD([sQuery(id+"F2.wireOp",EDGE,"E4.1.12"),sQuery(id+"F2.wireOp",EDGE,"E4.1.13"),sQuery(id+"F2.wireOp",EDGE,"E4.1.25"),sQuery(id+"F2.wireOp",EDGE,"E4.1.36")])],"isStart":true}),makeQuery(id+"F3.opExtrude","CAP_FACE",FACE,{"disambiguationData":[OSD([sQuery(id+"F2.wireOp",EDGE,"E4.1.14"),sQuery(id+"F2.wireOp",EDGE,"E4.1.15"),sQuery(id+"F2.wireOp",EDGE,"E4.1.37"),sQuery(id+"F2.wireOp",EDGE,"E4.1.41")])],"isStart":true}),makeQuery(id+"F3.opExtrude","CAP_FACE",FACE,{"disambiguationData":[OSD([sQuery(id+"F2.wireOp",EDGE,"E4.1.18"),sQuery(id+"F2.wireOp",EDGE,"E4.1.19"),sQuery(id+"F2.wireOp",EDGE,"E4.1.20"),sQuery(id+"F2.wireOp",EDGE,"E4.1.38")])],"isStart":true}),makeQuery(id+"F3.opExtrude","CAP_FACE",FACE,{"disambiguationData":[OSD([sQuery(id+"F2.wireOp",EDGE,"E4.1.21"),sQuery(id+"F2.wireOp",EDGE,"E4.1.22"),sQuery(id+"F2.wireOp",EDGE,"E4.1.23"),sQuery(id+"F2.wireOp",EDGE,"E4.1.39")])],"isStart":true}),makeQuery(id+"F3.opExtrude","CAP_FACE",FACE,{"disambiguationData":[OSD([sQuery(id+"F2.wireOp",EDGE,"E4.2.0"),sQuery(id+"F2.wireOp",EDGE,"E4.2.7"),sQuery(id+"F2.wireOp",EDGE,"E4.2.24"),sQuery(id+"F2.wireOp",EDGE,"E4.2.31")])],"isStart":true}),makeQuery(id+"F3.opExtrude","CAP_FACE",FACE,{"disambiguationData":[OSD([sQuery(id+"F2.wireOp",EDGE,"E4.2.1"),sQuery(id+"F2.wireOp",EDGE,"E4.2.6"),sQuery(id+"F2.wireOp",EDGE,"E4.2.27"),sQuery(id+"F2.wireOp",EDGE,"E4.2.33")])],"isStart":true}),makeQuery(id+"F3.opExtrude","CAP_FACE",FACE,{"disambiguationData":[OSD([sQuery(id+"F2.wireOp",EDGE,"E4.2.2"),sQuery(id+"F2.wireOp",EDGE,"E4.2.8"),sQuery(id+"F2.wireOp",EDGE,"E4.2.28"),sQuery(id+"F2.wireOp",EDGE,"E4.2.34")])],"isStart":true}),makeQuery(id+"F3.opExtrude","CAP_FACE",FACE,{"disambiguationData":[OSD([sQuery(id+"F2.wireOp",EDGE,"E4.2.3"),sQuery(id+"F2.wireOp",EDGE,"E4.2.9"),sQuery(id+"F2.wireOp",EDGE,"E4.2.16"),sQuery(id+"F2.wireOp",EDGE,"E4.2.29")])],"isStart":true}),makeQuery(id+"F3.opExtrude","CAP_FACE",FACE,{"disambiguationData":[OSD([sQuery(id+"F2.wireOp",EDGE,"E4.2.4"),sQuery(id+"F2.wireOp",EDGE,"E4.2.10"),sQuery(id+"F2.wireOp",EDGE,"E4.2.17"),sQuery(id+"F2.wireOp",EDGE,"E4.2.30")])],"isStart":true}),makeQuery(id+"F3.opExtrude","CAP_FACE",FACE,{"disambiguationData":[OSD([sQuery(id+"F2.wireOp",EDGE,"E4.2.11"),sQuery(id+"F2.wireOp",EDGE,"E4.2.26"),sQuery(id+"F2.wireOp",EDGE,"E4.2.32"),sQuery(id+"F2.wireOp",EDGE,"E4.2.35")])],"isStart":true}),makeQuery(id+"F3.opExtrude","CAP_FACE",FACE,{"disambiguationData":[OSD([sQuery(id+"F2.wireOp",EDGE,"E4.2.12"),sQuery(id+"F2.wireOp",EDGE,"E4.2.13"),sQuery(id+"F2.wireOp",EDGE,"E4.2.25"),sQuery(id+"F2.wireOp",EDGE,"E4.2.36")])],"isStart":true}),makeQuery(id+"F3.opExtrude","CAP_FACE",FACE,{"disambiguationData":[OSD([sQuery(id+"F2.wireOp",EDGE,"E4.2.14"),sQuery(id+"F2.wireOp",EDGE,"E4.2.15"),sQuery(id+"F2.wireOp",EDGE,"E4.2.37"),sQuery(id+"F2.wireOp",EDGE,"E4.2.41")])],"isStart":true}),makeQuery(id+"F3.opExtrude","CAP_FACE",FACE,{"disambiguationData":[OSD([sQuery(id+"F2.wireOp",EDGE,"E4.2.18"),sQuery(id+"F2.wireOp",EDGE,"E4.2.19"),sQuery(id+"F2.wireOp",EDGE,"E4.2.20"),sQuery(id+"F2.wireOp",EDGE,"E4.2.38")])],"isStart":true}),makeQuery(id+"F3.opExtrude","CAP_FACE",FACE,{"disambiguationData":[OSD([sQuery(id+"F2.wireOp",EDGE,"E4.2.21"),sQuery(id+"F2.wireOp",EDGE,"E4.2.22"),sQuery(id+"F2.wireOp",EDGE,"E4.2.23"),sQuery(id+"F2.wireOp",EDGE,"E4.2.39")])],"isStart":true}),makeQuery(id+"F3.opExtrude","CAP_FACE",FACE,{"disambiguationData":[OSD([sQuery(id+"F2.wireOp",EDGE,"E4.3.0"),sQuery(id+"F2.wireOp",EDGE,"E4.3.7"),sQuery(id+"F2.wireOp",EDGE,"E4.3.24"),sQuery(id+"F2.wireOp",EDGE,"E4.3.31")])],"isStart":true}),makeQuery(id+"F3.opExtrude","CAP_FACE",FACE,{"disambiguationData":[OSD([sQuery(id+"F2.wireOp",EDGE,"E4.3.1"),sQuery(id+"F2.wireOp",EDGE,"E4.3.6"),sQuery(id+"F2.wireOp",EDGE,"E4.3.27"),sQuery(id+"F2.wireOp",EDGE,"E4.3.33")])],"isStart":true}),makeQuery(id+"F3.opExtrude","CAP_FACE",FACE,{"disambiguationData":[OSD([sQuery(id+"F2.wireOp",EDGE,"E4.3.2"),sQuery(id+"F2.wireOp",EDGE,"E4.3.8"),sQuery(id+"F2.wireOp",EDGE,"E4.3.28"),sQuery(id+"F2.wireOp",EDGE,"E4.3.34")])],"isStart":true}),makeQuery(id+"F3.opExtrude","CAP_FACE",FACE,{"disambiguationData":[OSD([sQuery(id+"F2.wireOp",EDGE,"E4.3.3"),sQuery(id+"F2.wireOp",EDGE,"E4.3.9"),sQuery(id+"F2.wireOp",EDGE,"E4.3.16"),sQuery(id+"F2.wireOp",EDGE,"E4.3.29")])],"isStart":true}),makeQuery(id+"F3.opExtrude","CAP_FACE",FACE,{"disambiguationData":[OSD([sQuery(id+"F2.wireOp",EDGE,"E4.3.4"),sQuery(id+"F2.wireOp",EDGE,"E4.3.10"),sQuery(id+"F2.wireOp",EDGE,"E4.3.17"),sQuery(id+"F2.wireOp",EDGE,"E4.3.30")])],"isStart":true}),makeQuery(id+"F3.opExtrude","CAP_FACE",FACE,{"disambiguationData":[OSD([sQuery(id+"F2.wireOp",EDGE,"E4.3.11"),sQuery(id+"F2.wireOp",EDGE,"E4.3.26"),sQuery(id+"F2.wireOp",EDGE,"E4.3.32"),sQuery(id+"F2.wireOp",EDGE,"E4.3.35")])],"isStart":true}),makeQuery(id+"F3.opExtrude","CAP_FACE",FACE,{"disambiguationData":[OSD([sQuery(id+"F2.wireOp",EDGE,"E4.3.12"),sQuery(id+"F2.wireOp",EDGE,"E4.3.13"),sQuery(id+"F2.wireOp",EDGE,"E4.3.25"),sQuery(id+"F2.wireOp",EDGE,"E4.3.36")])],"isStart":true}),makeQuery(id+"F3.opExtrude","CAP_FACE",FACE,{"disambiguationData":[OSD([sQuery(id+"F2.wireOp",EDGE,"E4.3.14"),sQuery(id+"F2.wireOp",EDGE,"E4.3.15"),sQuery(id+"F2.wireOp",EDGE,"E4.3.37"),sQuery(id+"F2.wireOp",EDGE,"E4.3.41")])],"isStart":true}),makeQuery(id+"F3.opExtrude","CAP_FACE",FACE,{"disambiguationData":[OSD([sQuery(id+"F2.wireOp",EDGE,"E4.3.18"),sQuery(id+"F2.wireOp",EDGE,"E4.3.19"),sQuery(id+"F2.wireOp",EDGE,"E4.3.20"),sQuery(id+"F2.wireOp",EDGE,"E4.3.38")])],"isStart":true}),makeQuery(id+"F3.opExtrude","CAP_FACE",FACE,{"disambiguationData":[OSD([sQuery(id+"F2.wireOp",EDGE,"E4.3.21"),sQuery(id+"F2.wireOp",EDGE,"E4.3.22"),sQuery(id+"F2.wireOp",EDGE,"E4.3.23"),sQuery(id+"F2.wireOp",EDGE,"E4.3.39")])],"isStart":true})]});
            var sketch = newSketch(context, id + "F6", { "sketchPlane" : qUnion([Q0])});
            skLineSegment(sketch, "E8.bottom", {"start": v(-190, -203) * mm, "end": v(190, -203) * mm});
            skLineSegment(sketch, "E8.top", {"start": v(-190, -200) * mm, "end": v(190, -200) * mm});
            skLineSegment(sketch, "E8.left", {"start": v(-190, -203) * mm, "end": v(-190, -200) * mm});
            skLineSegment(sketch, "E8.right", {"start": v(190, -203) * mm, "end": v(190, -200) * mm});
            skSolve(sketch);
        }
        {
            var Q0;
            Q0 = qSketchRegion(id + "F6", true);
            extrude(context, id + "F7", {"entities" : qUnion([Q0]), "operationType" : NewBodyOperationType.REMOVE, "oppositeDirection" : true, "depth" : 25 * mm, "offsetDistance" : 25 * mm});
        }
    });
